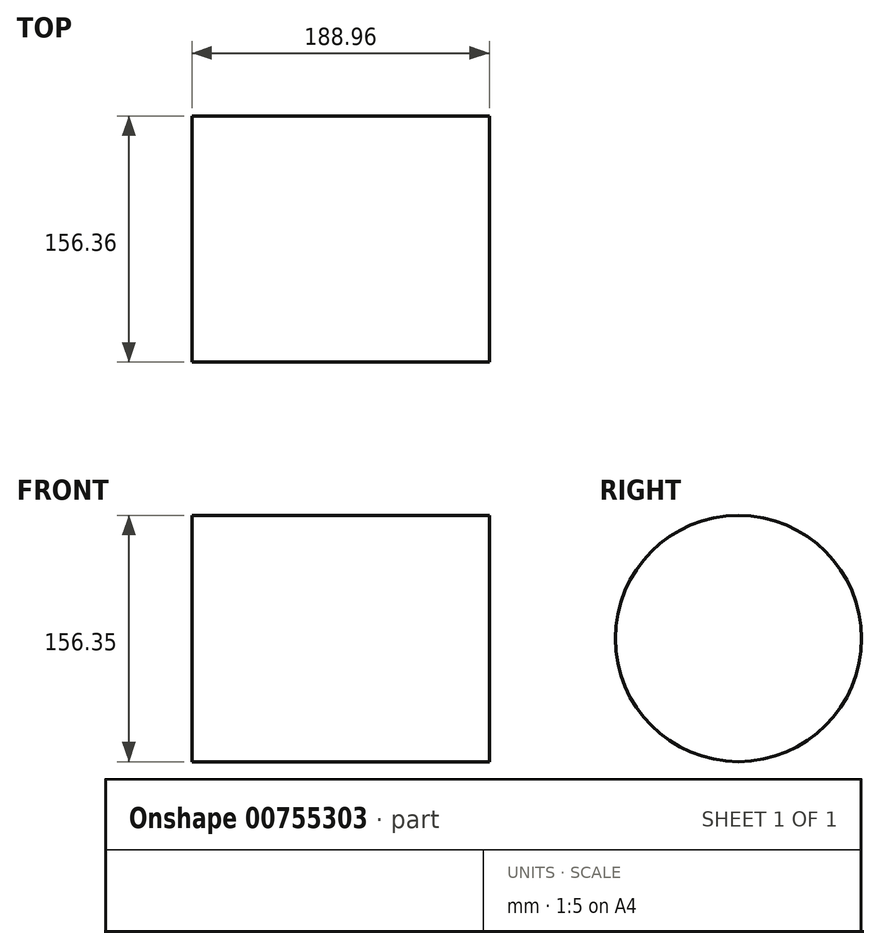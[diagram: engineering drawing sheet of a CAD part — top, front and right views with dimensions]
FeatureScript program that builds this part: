
annotation { "Feature Type Name" : "Feature", "Feature Type Description" : "" }
export const myFeature = defineFeature(function(context is Context, id is Id, definition is map)
    precondition{}
    {
        {
            var Q0;
            Q0=qCreatedBy(makeId("Front.planeOp"),FACE);
            var sketch = newSketch(context, id + "F0", { "sketchPlane" : qUnion([Q0])});
            skLineSegment(sketch, "E0.bottom", {"start": v(94.48, -39.09) * mm, "end": v(-94.48, -39.09) * mm});
            skLineSegment(sketch, "E0.top", {"start": v(94.48, 39.09) * mm, "end": v(-94.48, 39.09) * mm});
            skLineSegment(sketch, "E0.left", {"start": v(94.48, -39.09) * mm, "end": v(94.48, 39.09) * mm});
            skLineSegment(sketch, "E0.right", {"start": v(-94.48, -39.09) * mm, "end": v(-94.48, 39.09) * mm});
            skPoint(sketch, "E0.middle", {"position": v(0, 0) * mm});
            skSolve(sketch);
        }
        {
            var Q0;
            Q0=makeQuery(id+"F0.imprint","IMPRINT",FACE,{"disambiguationData":[TD([[makeQuery(id+"F0.imprint","IMPRINT",EDGE,{"derivedFrom":sQuery(id+"F0.wireOp",EDGE,"E0.bottom")}),-1.0]])]});
            var Q1;
            Q1=sQuery(id+"F0.wireOp",EDGE,"E0.bottom");
            revolve(context, id + "F1", {"surfaceOperationType" : NewSurfaceOperationType.NEW, "entities" : qUnion([Q0]), "axis" : qUnion([Q1]), "revolveType" : RevolveType.FULL});
        }
    });
